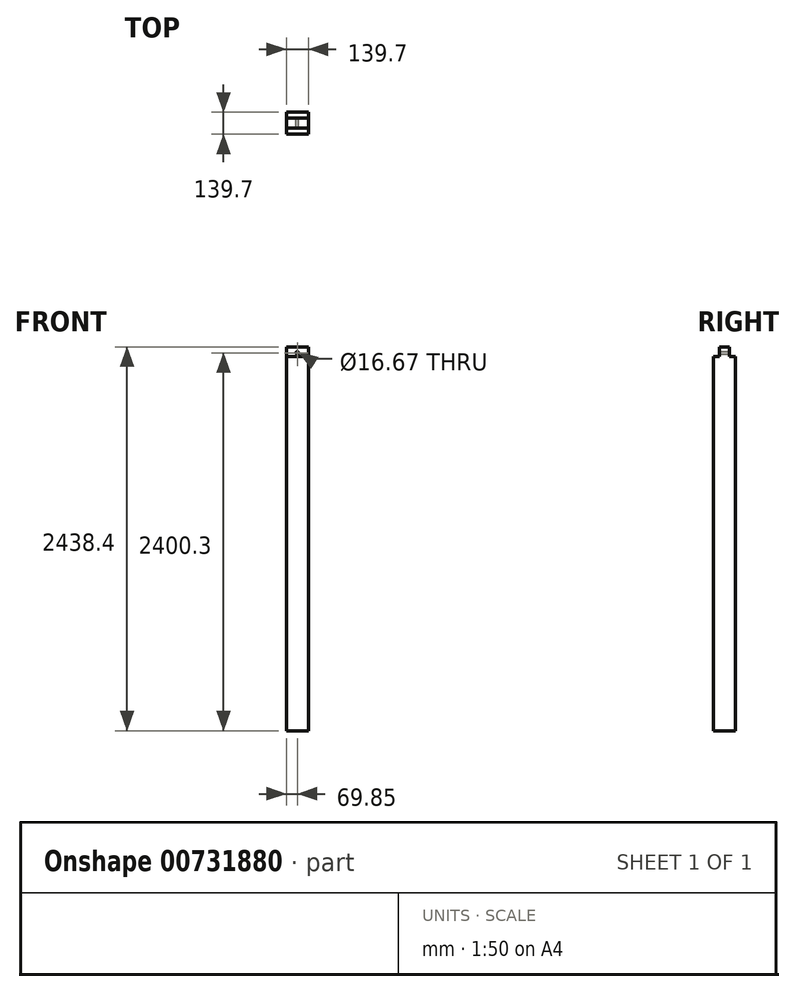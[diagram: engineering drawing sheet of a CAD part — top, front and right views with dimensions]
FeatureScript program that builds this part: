
annotation { "Feature Type Name" : "Feature", "Feature Type Description" : "" }
export const myFeature = defineFeature(function(context is Context, id is Id, definition is map)
    precondition{}
    {
        {
            var Q0;
            Q0=qCreatedBy(makeId("Top.planeOp"),FACE);
            var sketch = newSketch(context, id + "F0", { "sketchPlane" : qUnion([Q0])});
            skLineSegment(sketch, "E0.bottom", {"start": v(0, 0) * mm, "end": v(139.7, 0) * mm});
            skLineSegment(sketch, "E0.top", {"start": v(0, 139.7) * mm, "end": v(139.7, 139.7) * mm});
            skLineSegment(sketch, "E0.left", {"start": v(0, 0) * mm, "end": v(0, 139.7) * mm});
            skLineSegment(sketch, "E0.right", {"start": v(139.7, 0) * mm, "end": v(139.7, 139.7) * mm});
            skSolve(sketch);
        }
        {
            var Q0;
            Q0=makeQuery(id+"F0.imprint","IMPRINT",FACE,{"disambiguationData":[TD([[makeQuery(id+"F0.imprint","IMPRINT",EDGE,{"derivedFrom":sQuery(id+"F0.wireOp",EDGE,"E0.bottom")}),1.0]])]});
            extrude(context, id + "F1", {"entities" : qUnion([Q0]), "depth" : 2438.4 * mm, "offsetDistance" : 25.4 * mm});
        }
        {
            var Q0;
            Q0=makeQuery(id+"F1.opExtrude","SWEPT_FACE",FACE,{"disambiguationData":[OSD([sQuery(id+"F0.wireOp",EDGE,"E0.right")])]});
            var sketch = newSketch(context, id + "F2", { "sketchPlane" : qUnion([Q0])});
            skLineSegment(sketch, "E1.bottom", {"start": v(0, 2438.4) * mm, "end": v(38.1, 2438.4) * mm});
            skLineSegment(sketch, "E1.top", {"start": v(0, 2378.07) * mm, "end": v(38.1, 2378.07) * mm});
            skLineSegment(sketch, "E1.left", {"start": v(0, 2438.4) * mm, "end": v(0, 2378.07) * mm});
            skLineSegment(sketch, "E1.right", {"start": v(38.1, 2438.4) * mm, "end": v(38.1, 2378.07) * mm});
            skLineSegment(sketch, "E2.bottom", {"start": v(139.7, 2438.4) * mm, "end": v(101.6, 2438.4) * mm});
            skLineSegment(sketch, "E2.top", {"start": v(139.7, 2378.07) * mm, "end": v(101.6, 2378.07) * mm});
            skLineSegment(sketch, "E2.left", {"start": v(139.7, 2438.4) * mm, "end": v(139.7, 2378.07) * mm});
            skLineSegment(sketch, "E2.right", {"start": v(101.6, 2438.4) * mm, "end": v(101.6, 2378.07) * mm});
            skSolve(sketch);
        }
        {
            var Q0;
            Q0=makeQuery(id+"F2.imprint","IMPRINT",FACE,{"disambiguationData":[TD([[makeQuery(id+"F2.imprint","IMPRINT",EDGE,{"derivedFrom":sQuery(id+"F2.wireOp",EDGE,"E1.bottom")}),-1.0]])]});
            var Q1;
            Q1=makeQuery(id+"F2.imprint","IMPRINT",FACE,{"disambiguationData":[TD([[makeQuery(id+"F2.imprint","IMPRINT",EDGE,{"derivedFrom":sQuery(id+"F2.wireOp",EDGE,"E2.bottom")}),-1.0]])]});
            extrude(context, id + "F3", {"entities" : qUnion([Q0, Q1]), "operationType" : NewBodyOperationType.REMOVE, "endBound" : BoundingType.THROUGH_ALL, "oppositeDirection" : true, "depth" : 25.4 * mm, "offsetDistance" : 25.4 * mm});
        }
        {
            var Q0;
            Q0=makeQuery(id+"F1.opExtrude","SWEPT_FACE",FACE,{"disambiguationData":[OSD([sQuery(id+"F0.wireOp",EDGE,"E0.top")])]});
            var sketch = newSketch(context, id + "F4", { "sketchPlane" : qUnion([Q0])});
            skPoint(sketch, "E3", {"position": v(-69.85, 2378.07) * mm});
            skPoint(sketch, "E4", {"position": v(-69.85, 2400.3) * mm});
            skSolve(sketch);
        }
        {
            var Q0;
            Q0=sQuery(id+"F4.wireOp",VERTEX,"E4");
            var Q1;
            Q1=makeQuery(id+"F1.opExtrude","SWEPT_BODY",BODY,{"disambiguationData":[OSD([sQuery(id+"F0.wireOp",EDGE,"E0.bottom"),sQuery(id+"F0.wireOp",EDGE,"E0.top"),sQuery(id+"F0.wireOp",EDGE,"E0.left"),sQuery(id+"F0.wireOp",EDGE,"E0.right")])]});
            hole(context, id + "F5", {"style" : HoleStyle.SIMPLE, "endStyle" : HoleEndStyle.THROUGH, "standardTappedOrClearance" : lookupTablePath({ "fit" : "Normal (ASME)", "standard" : "ANSI", "size" : "5/8", "type" : "Clearance" }), "standardBlindInLast" : lookupTablePath({ "fit" : "Free", "standard" : "ANSI", "size" : "5/8", "type" : "Clearance" }), "holeDiameter" : 16.67 * mm, "majorDiameter" : 6.35 * mm, "isTappedThrough" : true, "tappedDepth" : 12.7 * mm, "tapClearance" : 3, "startFromSketch" : true, "locations" : qUnion([Q0]), "scope" : qUnion([Q1])});
        }
    });
